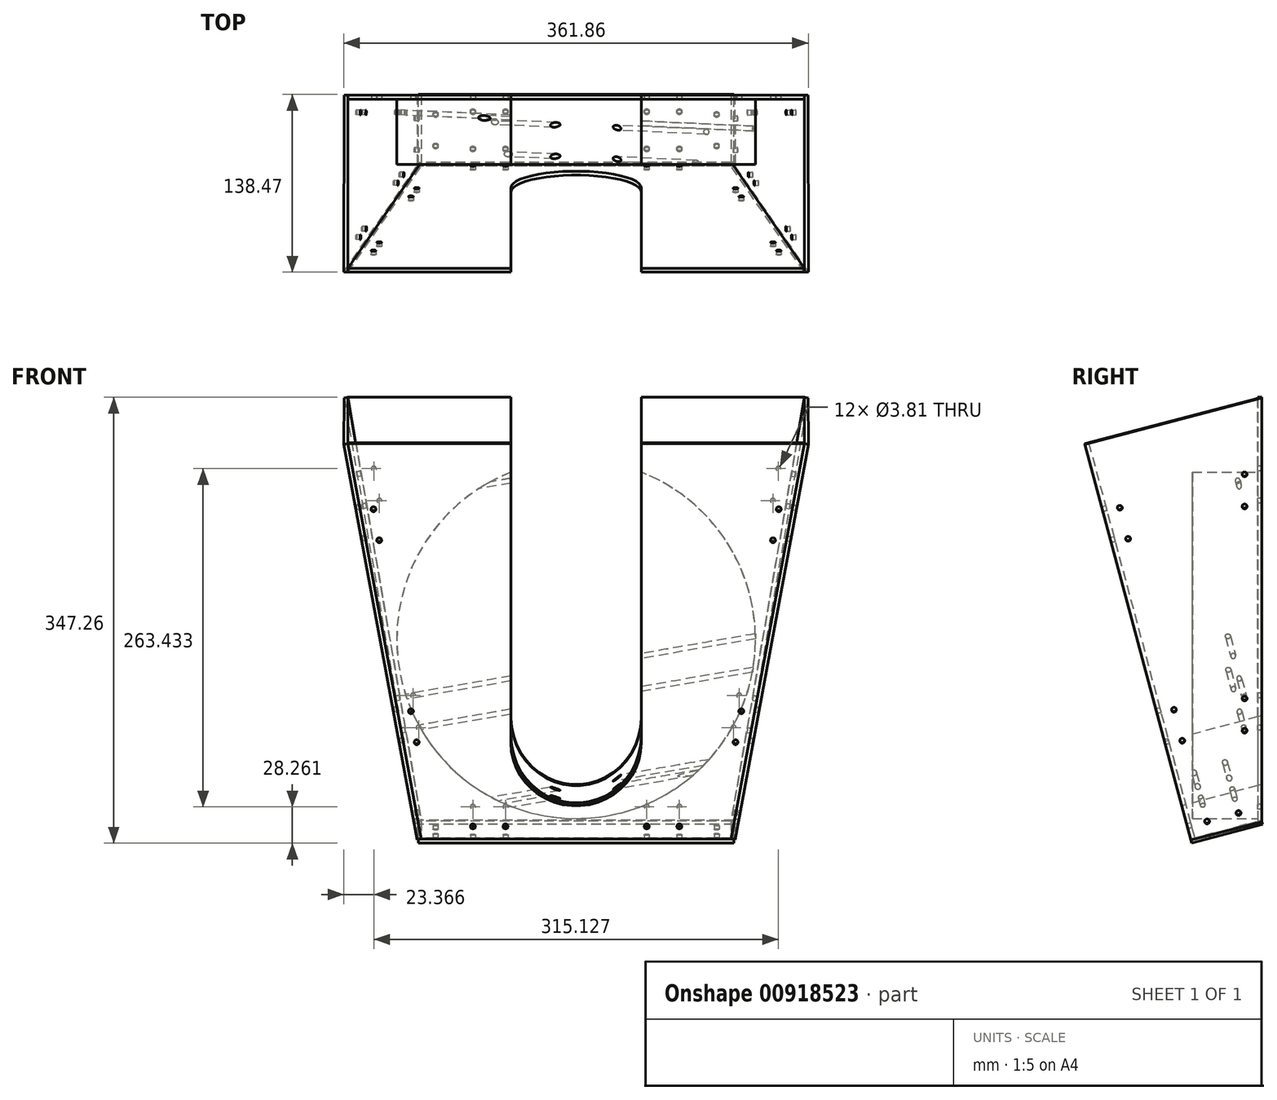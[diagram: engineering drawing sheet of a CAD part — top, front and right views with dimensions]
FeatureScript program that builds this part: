
annotation { "Feature Type Name" : "Feature", "Feature Type Description" : "" }
export const myFeature = defineFeature(function(context is Context, id is Id, definition is map)
    precondition{}
    {
        {
            var Q0;
            Q0=qCreatedBy(makeId("Right.planeOp"),FACE);
            var sketch = newSketch(context, id + "F0", { "sketchPlane" : qUnion([Q0])});
            skLineSegment(sketch, "E0.bottom", {"start": v(-164.52, 79.35) * mm, "end": v(-89.48, 66.12) * mm});
            skLineSegment(sketch, "E0.top", {"start": v(-67.49, 629.66) * mm, "end": v(7.56, 616.43) * mm});
            skLineSegment(sketch, "E0.left", {"start": v(-164.52, 79.35) * mm, "end": v(-67.49, 629.66) * mm});
            skLineSegment(sketch, "E0.right", {"start": v(-89.48, 66.12) * mm, "end": v(7.56, 616.43) * mm});
            skLineSegment(sketch, "E1.bottom", {"start": v(0, 38.1) * mm, "end": v(406.4, 38.1) * mm});
            skLineSegment(sketch, "E1.top", {"start": v(0, 546.1) * mm, "end": v(406.4, 546.1) * mm});
            skLineSegment(sketch, "E1.left", {"start": v(0, 38.1) * mm, "end": v(0, 546.1) * mm});
            skLineSegment(sketch, "E1.right", {"start": v(406.4, 38.1) * mm, "end": v(406.4, 546.1) * mm});
            skLineSegment(sketch, "E2.bottom", {"start": v(42.48, 128.48) * mm, "end": v(86.93, 128.48) * mm});
            skLineSegment(sketch, "E2.top", {"start": v(42.48, 84.03) * mm, "end": v(86.93, 84.03) * mm});
            skLineSegment(sketch, "E2.left", {"start": v(42.48, 128.48) * mm, "end": v(42.48, 84.03) * mm});
            skLineSegment(sketch, "E2.right", {"start": v(86.93, 128.48) * mm, "end": v(86.93, 84.03) * mm});
            skPoint(sketch, "E2.middle", {"position": v(64.7, 106.26) * mm});
            skSolve(sketch);
        }
        {
            var Q0;
            Q0=qCreatedBy(makeId("Front.planeOp"),FACE);
            var sketch = newSketch(context, id + "F1", { "sketchPlane" : qUnion([Q0])});
            skLineSegment(sketch, "E3.bottom", {"start": v(177.8, 596.9) * mm, "end": v(-177.8, 596.9) * mm});
            skLineSegment(sketch, "E3.top", {"start": v(120.65, 266.7) * mm, "end": v(-120.65, 266.7) * mm});
            skPoint(sketch, "E3.middle", {"position": v(0, 431.8) * mm});
            skLineSegment(sketch, "E4", {"start": v(-177.8, 596.9) * mm, "end": v(-120.65, 266.7) * mm});
            skLineSegment(sketch, "E5", {"start": v(0, 596.9) * mm, "end": v(0, 604.14) * mm, "construction": true});
            skPoint(sketch, "E5.endSnap0", {"position": v(0, 596.9) * mm});
            skLineSegment(sketch, "E6.MirrorCS", {"start": v(177.8, 596.9) * mm, "end": v(120.65, 266.7) * mm});
            skCircle(sketch, "E7", {"center": v(0, 408.44) * mm, "radius": 139.7 * mm, "construction": true});
            skCircle(sketch, "E8", {"center": v(0, 330.2) * mm, "radius": 17.46 * mm, "construction": true});
            skPoint(sketch, "E3.left.end.orphan", {"position": v(177.8, 266.7) * mm});
            skPoint(sketch, "E9.orphan", {"position": v(-177.8, 266.7) * mm});
            skSolve(sketch);
        }
        {
            var Q0;
            Q0=qSketchRegion(id+"F1",true);
            extrude(context, id + "F2", {"entities" : qUnion([Q0]), "oppositeDirection" : true, "depth" : 3.17 * mm});
        }
        {
            var Q0;
            Q0=makeQuery(id+"F1.imprint","IMPRINT",FACE,{"disambiguationData":[TD([[makeQuery(id+"F1.imprint","IMPRINT",EDGE,{"derivedFrom":sQuery(id+"F1.wireOp",EDGE,"E3.bottom")}),1.0]])]});
            var sketch = newSketch(context, id + "F3", { "sketchPlane" : qUnion([Q0])});
            skCircle(sketch, "E10.0", {"center": v(0, 408.44) * mm, "radius": 139.7 * mm});
            skSolve(sketch);
        }
        {
            var Q0;
            Q0=qSketchRegion(id+"F3",true);
            extrude(context, id + "F4", {"entities" : qUnion([Q0]), "depth" : 50.8 * mm});
        }
        {
            var Q0;
            Q0=makeQuery(id+"F4.opExtrude","CAP_FACE",FACE,{"disambiguationData":[OSD([sQuery(id+"F3.wireOp",EDGE,"E10.0")])],"isStart":false});
            var Q1;
            Q1=sQuery(id+"F1.wireOp",EDGE,"E3.top");
            cPlane(context, id + "F5", {"entities" : qUnion([Q0, Q1]), "cplaneType" : CPlaneType.LINE_ANGLE, "offset" : 25.4 * mm, "angle" : 345 * degree, "width" : 152.4 * mm, "height" : 152.4 * mm});
        }
        {
            var Q0;
            Q0=qCreatedBy(id+"F5.planeOp",FACE);
            cPlane(context, id + "F6", {"entities" : qUnion([Q0]), "cplaneType" : CPlaneType.OFFSET, "offset" : 53.97 * mm, "oppositeDirection" : true, "width" : 152.4 * mm, "height" : 152.4 * mm});
        }
        {
            var Q0;
            Q0=qCreatedBy(id+"F6.planeOp",FACE);
            var sketch = newSketch(context, id + "F7", { "sketchPlane" : qUnion([Q0])});
            skLineSegment(sketch, "E11.0", {"start": v(177.8, 576.56) * mm, "end": v(120.65, 257.61) * mm});
            skLineSegment(sketch, "E11.1", {"start": v(-177.8, 576.56) * mm, "end": v(177.8, 576.56) * mm});
            skLineSegment(sketch, "E11.2", {"start": v(-177.8, 576.56) * mm, "end": v(-120.65, 257.61) * mm});
            skLineSegment(sketch, "E11.3", {"start": v(-120.65, 257.61) * mm, "end": v(120.65, 257.61) * mm});
            skSolve(sketch);
        }
        {
            var Q0;
            Q0=makeQuery(id+"F7.imprint","IMPRINT",FACE,{"disambiguationData":[TD([[makeQuery(id+"F7.imprint","IMPRINT",EDGE,{"derivedFrom":sQuery(id+"F7.wireOp",EDGE,"E11.0")}),-1.0]])]});
            extrude(context, id + "F8", {"entities" : qUnion([Q0]), "depth" : 3.17 * mm});
        }
        {
            var Q0;
            Q0=makeQuery(id+"F8.opExtrude","SWEPT_FACE",FACE,{"disambiguationData":[OSD([sQuery(id+"F7.wireOp",EDGE,"E11.0")])]});
            var sketch = newSketch(context, id + "F9", { "sketchPlane" : qUnion([Q0])});
            skLineSegment(sketch, "E12.0", {"start": v(0.18, 618.48) * mm, "end": v(0.18, 283.37) * mm});
            skLineSegment(sketch, "E13.0", {"start": v(138.18, 582.92) * mm, "end": v(55.54, 269.6) * mm});
            skLineSegment(sketch, "E14", {"start": v(0.18, 283.37) * mm, "end": v(52.47, 270.41) * mm});
            skLineSegment(sketch, "E15", {"start": v(0.18, 618.48) * mm, "end": v(138.18, 582.92) * mm});
            skSolve(sketch);
        }
        {
            var Q0;
            {var subQ0=sQuery(id+"F9.wireOp",EDGE,"E12.0");Q0=makeQuery(id+"F9.imprint","IMPRINT",FACE,{"disambiguationData":[TD([[makeQuery(id+"F9.imprint","IMPRINT",EDGE,{"derivedFrom":subQ0}),1.0]])]});}
            var Q1;
            {var subQ0=sQuery(id+"F9.wireOp",EDGE,"E13.0");Q1=makeQuery(id+"F9.imprint","IMPRINT",FACE,{"disambiguationData":[TD([[makeQuery(id+"F9.imprint","IMPRINT",EDGE,{"derivedFrom":subQ0}),-1.0]])]});}
            extrude(context, id + "F10", {"entities" : qUnion([Q0, Q1]), "depth" : 3.17 * mm});
        }
        {
            var Q0;
            Q0=makeQuery(id+"F10.opExtrude","SWEPT_BODY",BODY,{"disambiguationData":[OSD([sQuery(id+"F7.wireOp",EDGE,"E11.0"),sQuery(id+"F9.wireOp",EDGE,"E12.0"),sQuery(id+"F9.wireOp",EDGE,"E14"),sQuery(id+"F9.wireOp",EDGE,"E15")])]});
            var Q1;
            Q1=qCreatedBy(makeId("Right.planeOp"),FACE);
            mirror(context, id + "F11", {"entities" : qUnion([Q0]), "mirrorPlane" : qUnion([Q1])});
        }
        {
            var Q0;
            Q0=makeQuery(id+"F8.opExtrude","SWEPT_FACE",FACE,{"disambiguationData":[OSD([sQuery(id+"F7.wireOp",EDGE,"E11.3")])]});
            var sketch = newSketch(context, id + "F12", { "sketchPlane" : qUnion([Q0])});
            skLineSegment(sketch, "E16.bottom", {"start": v(122.9, -15.05) * mm, "end": v(-122.9, -15.05) * mm});
            skLineSegment(sketch, "E16.top", {"start": v(122.9, -72.1) * mm, "end": v(-122.9, -72.1) * mm});
            skLineSegment(sketch, "E16.left", {"start": v(122.9, -15.05) * mm, "end": v(122.9, -72.1) * mm});
            skLineSegment(sketch, "E16.right", {"start": v(-122.9, -15.05) * mm, "end": v(-122.9, -72.1) * mm});
            skPoint(sketch, "E16.middle", {"position": v(0, -43.57) * mm});
            skSolve(sketch);
        }
        {
            var Q0;
            Q0=qSketchRegion(id+"F12",true);
            extrude(context, id + "F13", {"entities" : qUnion([Q0]), "depth" : 3.17 * mm});
        }
        {
            var Q0;
            Q0=makeQuery(id+"F8.opExtrude","CAP_FACE",FACE,{"disambiguationData":[OSD([sQuery(id+"F7.wireOp",EDGE,"E11.0"),sQuery(id+"F7.wireOp",EDGE,"E11.1"),sQuery(id+"F7.wireOp",EDGE,"E11.2"),sQuery(id+"F7.wireOp",EDGE,"E11.3")])],"isStart":true});
            var sketch = newSketch(context, id + "F14", { "sketchPlane" : qUnion([Q0])});
            skLineSegment(sketch, "E17", {"start": v(0, 439.09) * mm, "end": v(0, 333.36) * mm, "construction": true});
            skLineSegment(sketch, "E18.bottom", {"start": v(-170.23, 534.32) * mm, "end": v(-149.92, 537.96) * mm, "construction": true});
            skLineSegment(sketch, "E18.top", {"start": v(-161.27, 484.32) * mm, "end": v(-140.96, 487.96) * mm, "construction": true});
            skLineSegment(sketch, "E18.left", {"start": v(-170.23, 534.32) * mm, "end": v(-161.27, 484.32) * mm, "construction": true});
            skLineSegment(sketch, "E18.right", {"start": v(-149.92, 537.96) * mm, "end": v(-140.96, 487.96) * mm, "construction": true});
            skLineSegment(sketch, "E19.bottom", {"start": v(-93.12, 278.25) * mm, "end": v(-42.32, 278.25) * mm, "construction": true});
            skLineSegment(sketch, "E19.top", {"start": v(-93.12, 257.61) * mm, "end": v(-42.32, 257.61) * mm});
            skLineSegment(sketch, "E19.left", {"start": v(-93.12, 278.25) * mm, "end": v(-93.12, 257.61) * mm, "construction": true});
            skLineSegment(sketch, "E19.right", {"start": v(-42.32, 278.25) * mm, "end": v(-42.32, 257.61) * mm, "construction": true});
            skLineSegment(sketch, "E20", {"start": v(-160.07, 536.14) * mm, "end": v(-151.11, 486.14) * mm, "construction": true});
            skLineSegment(sketch, "E21", {"start": v(-93.12, 267.93) * mm, "end": v(-42.32, 267.93) * mm, "construction": true});
            skLineSegment(sketch, "E22", {"start": v(-145.44, 512.96) * mm, "end": v(-165.75, 509.32) * mm, "construction": true});
            skLineSegment(sketch, "E23", {"start": v(-67.72, 278.25) * mm, "end": v(-67.72, 257.61) * mm, "construction": true});
            skCircle(sketch, "E24", {"center": v(-157.83, 523.64) * mm, "radius": 1.9 * mm});
            skCircle(sketch, "E25.MirrorC", {"center": v(-153.35, 498.64) * mm, "radius": 1.9 * mm});
            skLineSegment(sketch, "E26.bottom", {"start": v(-141.04, 371.42) * mm, "end": v(-120.73, 375.06) * mm, "construction": true});
            skLineSegment(sketch, "E26.top", {"start": v(-132.08, 321.41) * mm, "end": v(-111.77, 325.05) * mm, "construction": true});
            skLineSegment(sketch, "E26.left", {"start": v(-141.04, 371.42) * mm, "end": v(-132.08, 321.41) * mm, "construction": true});
            skLineSegment(sketch, "E26.right", {"start": v(-120.73, 375.06) * mm, "end": v(-111.77, 325.05) * mm, "construction": true});
            skLineSegment(sketch, "E27", {"start": v(-130.88, 373.24) * mm, "end": v(-121.92, 323.23) * mm, "construction": true});
            skLineSegment(sketch, "E28", {"start": v(-116.25, 350.05) * mm, "end": v(-136.56, 346.41) * mm, "construction": true});
            skCircle(sketch, "E29", {"center": v(-128.64, 360.73) * mm, "radius": 1.9 * mm});
            skCircle(sketch, "E30.MirrorC", {"center": v(-124.16, 335.73) * mm, "radius": 1.9 * mm});
            skCircle(sketch, "E31", {"center": v(-80.42, 267.93) * mm, "radius": 1.9 * mm});
            skCircle(sketch, "E32.MirrorC", {"center": v(-55.02, 267.93) * mm, "radius": 1.9 * mm});
            skLineSegment(sketch, "E33.MirrorCS", {"start": v(132.08, 321.41) * mm, "end": v(111.77, 325.05) * mm, "construction": true});
            skCircle(sketch, "E34.MirrorC", {"center": v(128.64, 360.73) * mm, "radius": 1.9 * mm});
            skCircle(sketch, "E35.MirrorC", {"center": v(157.83, 523.64) * mm, "radius": 1.9 * mm});
            skLineSegment(sketch, "E36.MirrorCS", {"start": v(42.32, 278.25) * mm, "end": v(42.32, 257.61) * mm, "construction": true});
            skLineSegment(sketch, "E37.MirrorCS", {"start": v(93.12, 278.25) * mm, "end": v(93.12, 257.61) * mm, "construction": true});
            skLineSegment(sketch, "E38.MirrorCS", {"start": v(161.27, 484.32) * mm, "end": v(140.96, 487.96) * mm, "construction": true});
            skCircle(sketch, "E39.MirrorC", {"center": v(55.02, 267.93) * mm, "radius": 1.9 * mm});
            skLineSegment(sketch, "E40.MirrorCS", {"start": v(145.44, 512.96) * mm, "end": v(165.75, 509.32) * mm, "construction": true});
            skLineSegment(sketch, "E41.MirrorCS", {"start": v(170.23, 534.32) * mm, "end": v(149.92, 537.96) * mm, "construction": true});
            skLineSegment(sketch, "E42.MirrorCS", {"start": v(130.88, 373.24) * mm, "end": v(121.92, 323.23) * mm, "construction": true});
            skCircle(sketch, "E43.MirrorC", {"center": v(124.16, 335.73) * mm, "radius": 1.9 * mm});
            skLineSegment(sketch, "E44.MirrorCS", {"start": v(160.07, 536.14) * mm, "end": v(151.11, 486.14) * mm, "construction": true});
            skLineSegment(sketch, "E45.MirrorCS", {"start": v(141.04, 371.42) * mm, "end": v(120.73, 375.06) * mm, "construction": true});
            skCircle(sketch, "E46.MirrorC", {"center": v(153.35, 498.64) * mm, "radius": 1.9 * mm});
            skCircle(sketch, "E47.MirrorC", {"center": v(80.42, 267.93) * mm, "radius": 1.9 * mm});
            skLineSegment(sketch, "E48.MirrorCS", {"start": v(141.04, 371.42) * mm, "end": v(132.08, 321.41) * mm, "construction": true});
            skLineSegment(sketch, "E49.MirrorCS", {"start": v(93.12, 257.61) * mm, "end": v(42.32, 257.61) * mm});
            skLineSegment(sketch, "E50.MirrorCS", {"start": v(116.25, 350.05) * mm, "end": v(136.56, 346.41) * mm, "construction": true});
            skLineSegment(sketch, "E51.MirrorCS", {"start": v(170.23, 534.32) * mm, "end": v(161.27, 484.32) * mm, "construction": true});
            skLineSegment(sketch, "E52.MirrorCS", {"start": v(149.92, 537.96) * mm, "end": v(140.96, 487.96) * mm, "construction": true});
            skLineSegment(sketch, "E53.MirrorCS", {"start": v(120.73, 375.06) * mm, "end": v(111.77, 325.05) * mm, "construction": true});
            skLineSegment(sketch, "E54.MirrorCS", {"start": v(93.12, 267.93) * mm, "end": v(42.32, 267.93) * mm, "construction": true});
            skLineSegment(sketch, "E55.MirrorCS", {"start": v(67.72, 278.25) * mm, "end": v(67.72, 257.61) * mm, "construction": true});
            skLineSegment(sketch, "E56.MirrorCS", {"start": v(93.12, 278.25) * mm, "end": v(42.32, 278.25) * mm, "construction": true});
            skSolve(sketch);
        }
        {
            var Q0;
            Q0=qSketchRegion(id+"F14",true);
            var Q1;
            Q1=makeQuery(id+"F8.opExtrude","CAP_FACE",FACE,{"disambiguationData":[OSD([sQuery(id+"F7.wireOp",EDGE,"E11.0"),sQuery(id+"F7.wireOp",EDGE,"E11.1"),sQuery(id+"F7.wireOp",EDGE,"E11.2"),sQuery(id+"F7.wireOp",EDGE,"E11.3")])],"isStart":false});
            extrude(context, id + "F15", {"entities" : qUnion([Q0]), "operationType" : NewBodyOperationType.REMOVE, "endBound" : BoundingType.UP_TO_SURFACE, "oppositeDirection" : true, "depth" : 25.4 * mm, "endBoundEntityFace" : qUnion([Q1]), "offsetDistance" : 25.4 * mm});
        }
        {
            var Q0;
            Q0=makeQuery(id+"F10.opExtrude","CAP_FACE",FACE,{"disambiguationData":[OSD([sQuery(id+"F7.wireOp",EDGE,"E11.0"),sQuery(id+"F7.wireOp",EDGE,"E11.3"),sQuery(id+"F9.wireOp",EDGE,"E12.0"),sQuery(id+"F9.wireOp",EDGE,"E13.0"),sQuery(id+"F9.wireOp",EDGE,"E14"),sQuery(id+"F9.wireOp",EDGE,"E15")])],"isStart":false});
            var sketch = newSketch(context, id + "F16", { "sketchPlane" : qUnion([Q0])});
            skLineSegment(sketch, "E57.0", {"start": v(127.23, 541.42) * mm, "end": v(114.28, 492.3) * mm, "construction": true});
            skLineSegment(sketch, "E58.0", {"start": v(85.03, 381.4) * mm, "end": v(72.07, 332.28) * mm, "construction": true});
            skLineSegment(sketch, "E59.bottom", {"start": v(62, 387.47) * mm, "end": v(85.03, 381.4) * mm, "construction": true});
            skLineSegment(sketch, "E59.top", {"start": v(49.05, 338.35) * mm, "end": v(72.07, 332.28) * mm, "construction": true});
            skLineSegment(sketch, "E59.left", {"start": v(62, 387.47) * mm, "end": v(49.05, 338.35) * mm, "construction": true});
            skLineSegment(sketch, "E60", {"start": v(81.96, 382.2) * mm, "end": v(69, 333.09) * mm, "construction": true});
            skPoint(sketch, "E61", {"position": v(71.98, 384.84) * mm});
            skLineSegment(sketch, "E62", {"start": v(71.98, 384.84) * mm, "end": v(59.02, 335.72) * mm, "construction": true});
            skLineSegment(sketch, "E63", {"start": v(55.52, 362.9) * mm, "end": v(75.48, 357.65) * mm, "construction": true});
            skCircle(sketch, "E64", {"center": v(62.26, 348) * mm, "radius": 1.9 * mm});
            skCircle(sketch, "E65.MirrorC", {"center": v(68.74, 372.56) * mm, "radius": 1.9 * mm});
            skLineSegment(sketch, "E66.bottom", {"start": v(104.2, 547.5) * mm, "end": v(127.23, 541.42) * mm, "construction": true});
            skLineSegment(sketch, "E66.top", {"start": v(91.25, 498.37) * mm, "end": v(114.28, 492.3) * mm, "construction": true});
            skLineSegment(sketch, "E66.left", {"start": v(104.2, 547.5) * mm, "end": v(91.25, 498.37) * mm, "construction": true});
            skLineSegment(sketch, "E67", {"start": v(124.16, 542.23) * mm, "end": v(111.2, 493.11) * mm, "construction": true});
            skPoint(sketch, "E68", {"position": v(114.18, 544.86) * mm});
            skLineSegment(sketch, "E69", {"start": v(114.18, 544.86) * mm, "end": v(101.23, 495.74) * mm, "construction": true});
            skLineSegment(sketch, "E70", {"start": v(97.73, 522.93) * mm, "end": v(117.68, 517.67) * mm, "construction": true});
            skCircle(sketch, "E71", {"center": v(104.47, 508.02) * mm, "radius": 1.9 * mm});
            skCircle(sketch, "E72.MirrorC", {"center": v(110.95, 532.58) * mm, "radius": 1.9 * mm});
            skLineSegment(sketch, "E73.bottom", {"start": v(3.35, 570.93) * mm, "end": v(24, 570.93) * mm, "construction": true});
            skLineSegment(sketch, "E73.top", {"start": v(3.35, 520.13) * mm, "end": v(24, 520.13) * mm, "construction": true});
            skLineSegment(sketch, "E73.left", {"start": v(3.35, 570.93) * mm, "end": v(3.35, 520.13) * mm, "construction": true});
            skLineSegment(sketch, "E73.right", {"start": v(24, 570.93) * mm, "end": v(24, 520.13) * mm, "construction": true});
            skLineSegment(sketch, "E74.bottom", {"start": v(3.35, 570.93) * mm, "end": v(0.18, 570.93) * mm, "construction": true});
            skLineSegment(sketch, "E74.top", {"start": v(3.35, 520.13) * mm, "end": v(0.18, 520.13) * mm, "construction": true});
            skLineSegment(sketch, "E74.right", {"start": v(0.18, 570.93) * mm, "end": v(0.18, 520.13) * mm, "construction": true});
            skLineSegment(sketch, "E75", {"start": v(13.67, 570.93) * mm, "end": v(13.67, 520.13) * mm, "construction": true});
            skLineSegment(sketch, "E76", {"start": v(24, 545.53) * mm, "end": v(3.35, 545.53) * mm, "construction": true});
            skCircle(sketch, "E77", {"center": v(13.67, 558.23) * mm, "radius": 1.9 * mm});
            skCircle(sketch, "E78.MirrorC", {"center": v(13.67, 532.83) * mm, "radius": 1.9 * mm});
            skLineSegment(sketch, "E79.bottom", {"start": v(3.35, 393.68) * mm, "end": v(24, 393.68) * mm, "construction": true});
            skLineSegment(sketch, "E79.top", {"start": v(3.35, 342.88) * mm, "end": v(24, 342.88) * mm, "construction": true});
            skLineSegment(sketch, "E79.left", {"start": v(3.35, 393.68) * mm, "end": v(3.35, 342.88) * mm, "construction": true});
            skLineSegment(sketch, "E79.right", {"start": v(24, 393.68) * mm, "end": v(24, 342.88) * mm, "construction": true});
            skLineSegment(sketch, "E80.bottom", {"start": v(3.35, 393.68) * mm, "end": v(0.18, 393.68) * mm, "construction": true});
            skLineSegment(sketch, "E80.top", {"start": v(3.35, 342.88) * mm, "end": v(0.18, 342.88) * mm, "construction": true});
            skLineSegment(sketch, "E80.right", {"start": v(0.18, 393.68) * mm, "end": v(0.18, 342.88) * mm, "construction": true});
            skLineSegment(sketch, "E81", {"start": v(13.67, 393.68) * mm, "end": v(13.67, 342.88) * mm, "construction": true});
            skLineSegment(sketch, "E82", {"start": v(24, 368.28) * mm, "end": v(3.35, 368.28) * mm, "construction": true});
            skCircle(sketch, "E83", {"center": v(13.67, 380.98) * mm, "radius": 1.9 * mm});
            skCircle(sketch, "E84.MirrorC", {"center": v(13.67, 355.58) * mm, "radius": 1.9 * mm});
            skLineSegment(sketch, "E85.bottom", {"start": v(8.73, 303.76) * mm, "end": v(57.85, 290.8) * mm, "construction": true});
            skLineSegment(sketch, "E85.top", {"start": v(3.46, 283.8) * mm, "end": v(52.58, 270.85) * mm, "construction": true});
            skLineSegment(sketch, "E85.left", {"start": v(8.73, 303.76) * mm, "end": v(3.46, 283.8) * mm, "construction": true});
            skLineSegment(sketch, "E85.right", {"start": v(57.85, 290.8) * mm, "end": v(52.58, 270.85) * mm, "construction": true});
            skLineSegment(sketch, "E86.top", {"start": v(2.65, 280.73) * mm, "end": v(51.77, 267.78) * mm, "construction": true});
            skLineSegment(sketch, "E86.left", {"start": v(3.46, 283.8) * mm, "end": v(2.65, 280.73) * mm, "construction": true});
            skLineSegment(sketch, "E86.right", {"start": v(52.58, 270.85) * mm, "end": v(51.77, 267.78) * mm, "construction": true});
            skLineSegment(sketch, "E87", {"start": v(6.1, 293.78) * mm, "end": v(55.22, 280.82) * mm, "construction": true});
            skLineSegment(sketch, "E88", {"start": v(33.29, 297.28) * mm, "end": v(28.02, 277.32) * mm, "construction": true});
            skCircle(sketch, "E89", {"center": v(18.38, 290.54) * mm, "radius": 1.9 * mm});
            skCircle(sketch, "E90.MirrorC", {"center": v(42.94, 284.06) * mm, "radius": 1.9 * mm});
            skSolve(sketch);
        }
        {
            var Q0;
            Q0=qSketchRegion(id+"F16",true);
            extrude(context, id + "F17", {"entities" : qUnion([Q0]), "operationType" : NewBodyOperationType.REMOVE, "endBound" : BoundingType.THROUGH_ALL, "oppositeDirection" : true, "depth" : 25.4 * mm, "offsetDistance" : 25.4 * mm});
        }
        {
            var Q0;
            Q0=makeQuery(id+"F11.opPattern","COPY",BODY,{"derivedFrom":makeQuery(id+"F10.opExtrude","SWEPT_BODY",BODY,{"disambiguationData":[OSD([sQuery(id+"F7.wireOp",EDGE,"E11.0"),sQuery(id+"F7.wireOp",EDGE,"E11.3"),sQuery(id+"F9.wireOp",EDGE,"E12.0"),sQuery(id+"F9.wireOp",EDGE,"E13.0"),sQuery(id+"F9.wireOp",EDGE,"E14"),sQuery(id+"F9.wireOp",EDGE,"E15")])]}),"instanceName":"1"});
            deleteBodies(context, id + "F18", {"entities" : qUnion([Q0])});
        }
        {
            var Q0;
            Q0=makeQuery(id+"F10.opExtrude","SWEPT_BODY",BODY,{"disambiguationData":[OSD([sQuery(id+"F7.wireOp",EDGE,"E11.0"),sQuery(id+"F7.wireOp",EDGE,"E11.3"),sQuery(id+"F9.wireOp",EDGE,"E12.0"),sQuery(id+"F9.wireOp",EDGE,"E13.0"),sQuery(id+"F9.wireOp",EDGE,"E14"),sQuery(id+"F9.wireOp",EDGE,"E15")])]});
            var Q1;
            Q1=qCreatedBy(makeId("Right.planeOp"),FACE);
            mirror(context, id + "F19", {"entities" : qUnion([Q0]), "mirrorPlane" : qUnion([Q1])});
        }
        {
            var Q0;
            Q0=makeQuery(id+"F1.imprint","IMPRINT",FACE,{"disambiguationData":[TD([[makeQuery(id+"F1.imprint","IMPRINT",EDGE,{"derivedFrom":sQuery(id+"F1.wireOp",EDGE,"E3.bottom")}),1.0]])]});
            var sketch = newSketch(context, id + "F20", { "sketchPlane" : qUnion([Q0])});
            skLineSegment(sketch, "E91.0", {"start": v(-172.82, 549.5) * mm, "end": v(-164.15, 499.45) * mm, "construction": true});
            skLineSegment(sketch, "E92.bottom", {"start": v(-169.9, 552.1) * mm, "end": v(-173.03, 551.57) * mm, "construction": true});
            skLineSegment(sketch, "E92.top", {"start": v(-161.23, 502.05) * mm, "end": v(-164.36, 501.51) * mm, "construction": true});
            skLineSegment(sketch, "E92.left", {"start": v(-169.9, 552.1) * mm, "end": v(-161.23, 502.05) * mm, "construction": true});
            skLineSegment(sketch, "E92.right", {"start": v(-173.03, 551.57) * mm, "end": v(-164.36, 501.51) * mm, "construction": true});
            skLineSegment(sketch, "E93.bottom", {"start": v(-149.56, 555.63) * mm, "end": v(-169.9, 552.1) * mm, "construction": true});
            skLineSegment(sketch, "E93.top", {"start": v(-140.9, 505.57) * mm, "end": v(-161.23, 502.05) * mm, "construction": true});
            skLineSegment(sketch, "E93.left", {"start": v(-149.56, 555.63) * mm, "end": v(-140.9, 505.57) * mm, "construction": true});
            skLineSegment(sketch, "E94", {"start": v(-159.73, 553.87) * mm, "end": v(-151.07, 503.81) * mm, "construction": true});
            skLineSegment(sketch, "E95", {"start": v(-145.23, 530.6) * mm, "end": v(-165.57, 527.08) * mm, "construction": true});
            skCircle(sketch, "E96", {"center": v(-157.56, 541.35) * mm, "radius": 1.9 * mm});
            skCircle(sketch, "E97.MirrorC", {"center": v(-153.23, 516.33) * mm, "radius": 1.9 * mm});
            skLineSegment(sketch, "E98", {"start": v(0, 542.09) * mm, "end": v(0, 433.89) * mm, "construction": true});
            skLineSegment(sketch, "E99.0", {"start": v(-137.98, 349.1) * mm, "end": v(-129.32, 299.04) * mm, "construction": true});
            skLineSegment(sketch, "E100.bottom", {"start": v(-139.32, 375.42) * mm, "end": v(-142.45, 374.88) * mm, "construction": true});
            skLineSegment(sketch, "E100.top", {"start": v(-130.65, 325.37) * mm, "end": v(-133.78, 324.83) * mm, "construction": true});
            skLineSegment(sketch, "E100.left", {"start": v(-139.32, 375.42) * mm, "end": v(-130.65, 325.37) * mm, "construction": true});
            skLineSegment(sketch, "E100.right", {"start": v(-142.45, 374.88) * mm, "end": v(-133.78, 324.83) * mm, "construction": true});
            skLineSegment(sketch, "E101.bottom", {"start": v(-118.98, 378.94) * mm, "end": v(-139.32, 375.42) * mm, "construction": true});
            skLineSegment(sketch, "E101.top", {"start": v(-110.32, 328.89) * mm, "end": v(-130.65, 325.37) * mm, "construction": true});
            skLineSegment(sketch, "E101.left", {"start": v(-118.98, 378.94) * mm, "end": v(-110.32, 328.89) * mm, "construction": true});
            skLineSegment(sketch, "E102", {"start": v(-129.15, 377.18) * mm, "end": v(-120.49, 327.13) * mm, "construction": true});
            skLineSegment(sketch, "E103", {"start": v(-114.65, 353.92) * mm, "end": v(-134.99, 350.4) * mm, "construction": true});
            skCircle(sketch, "E104", {"center": v(-126.98, 364.67) * mm, "radius": 1.9 * mm});
            skCircle(sketch, "E105.MirrorC", {"center": v(-122.65, 339.64) * mm, "radius": 1.9 * mm});
            skLineSegment(sketch, "E106.bottom", {"start": v(-42.32, 288.24) * mm, "end": v(-93.12, 288.24) * mm, "construction": true});
            skLineSegment(sketch, "E106.top", {"start": v(-42.32, 267.6) * mm, "end": v(-93.12, 267.6) * mm, "construction": true});
            skLineSegment(sketch, "E106.left", {"start": v(-42.32, 288.24) * mm, "end": v(-42.32, 267.6) * mm, "construction": true});
            skLineSegment(sketch, "E106.right", {"start": v(-93.12, 288.24) * mm, "end": v(-93.12, 267.6) * mm, "construction": true});
            skLineSegment(sketch, "E107.top", {"start": v(-42.32, 264.43) * mm, "end": v(-93.12, 264.43) * mm, "construction": true});
            skLineSegment(sketch, "E107.left", {"start": v(-42.32, 267.6) * mm, "end": v(-42.32, 264.43) * mm, "construction": true});
            skLineSegment(sketch, "E107.right", {"start": v(-93.12, 267.6) * mm, "end": v(-93.12, 264.43) * mm, "construction": true});
            skLineSegment(sketch, "E108", {"start": v(-42.32, 277.92) * mm, "end": v(-93.12, 277.92) * mm, "construction": true});
            skLineSegment(sketch, "E109", {"start": v(-67.72, 288.24) * mm, "end": v(-67.72, 267.6) * mm, "construction": true});
            skCircle(sketch, "E110", {"center": v(-55.02, 277.92) * mm, "radius": 1.9 * mm});
            skCircle(sketch, "E111.MirrorC", {"center": v(-80.42, 277.92) * mm, "radius": 1.9 * mm});
            skLineSegment(sketch, "E112.MirrorCS", {"start": v(161.23, 502.05) * mm, "end": v(164.36, 501.51) * mm, "construction": true});
            skLineSegment(sketch, "E113.MirrorCS", {"start": v(169.9, 552.1) * mm, "end": v(173.03, 551.57) * mm, "construction": true});
            skLineSegment(sketch, "E114.MirrorCS", {"start": v(139.32, 375.42) * mm, "end": v(142.45, 374.88) * mm, "construction": true});
            skLineSegment(sketch, "E115.MirrorCS", {"start": v(130.65, 325.37) * mm, "end": v(133.78, 324.83) * mm, "construction": true});
            skLineSegment(sketch, "E116.MirrorCS", {"start": v(42.32, 267.6) * mm, "end": v(42.32, 264.43) * mm, "construction": true});
            skLineSegment(sketch, "E117.MirrorCS", {"start": v(93.12, 267.6) * mm, "end": v(93.12, 264.43) * mm, "construction": true});
            skLineSegment(sketch, "E118.MirrorCS", {"start": v(139.32, 375.42) * mm, "end": v(130.65, 325.37) * mm, "construction": true});
            skCircle(sketch, "E119.MirrorC", {"center": v(126.98, 364.67) * mm, "radius": 1.9 * mm});
            skLineSegment(sketch, "E120.MirrorCS", {"start": v(169.9, 552.1) * mm, "end": v(161.23, 502.05) * mm, "construction": true});
            skLineSegment(sketch, "E121.MirrorCS", {"start": v(172.82, 549.5) * mm, "end": v(164.15, 499.45) * mm, "construction": true});
            skLineSegment(sketch, "E122.MirrorCS", {"start": v(142.45, 374.88) * mm, "end": v(133.78, 324.83) * mm, "construction": true});
            skLineSegment(sketch, "E123.MirrorCS", {"start": v(173.03, 551.57) * mm, "end": v(164.36, 501.51) * mm, "construction": true});
            skLineSegment(sketch, "E124.MirrorCS", {"start": v(42.32, 264.43) * mm, "end": v(93.12, 264.43) * mm, "construction": true});
            skLineSegment(sketch, "E125.MirrorCS", {"start": v(129.15, 377.18) * mm, "end": v(120.49, 327.13) * mm, "construction": true});
            skLineSegment(sketch, "E126.MirrorCS", {"start": v(42.32, 288.24) * mm, "end": v(42.32, 267.6) * mm, "construction": true});
            skCircle(sketch, "E127.MirrorC", {"center": v(153.23, 516.33) * mm, "radius": 1.9 * mm});
            skLineSegment(sketch, "E128.MirrorCS", {"start": v(140.9, 505.57) * mm, "end": v(161.23, 502.05) * mm, "construction": true});
            skLineSegment(sketch, "E129.MirrorCS", {"start": v(149.56, 555.63) * mm, "end": v(169.9, 552.1) * mm, "construction": true});
            skLineSegment(sketch, "E130.MirrorCS", {"start": v(145.23, 530.6) * mm, "end": v(165.57, 527.08) * mm, "construction": true});
            skLineSegment(sketch, "E131.MirrorCS", {"start": v(118.98, 378.94) * mm, "end": v(110.32, 328.89) * mm, "construction": true});
            skLineSegment(sketch, "E132.MirrorCS", {"start": v(118.98, 378.94) * mm, "end": v(139.32, 375.42) * mm, "construction": true});
            skCircle(sketch, "E133.MirrorC", {"center": v(157.56, 541.35) * mm, "radius": 1.9 * mm});
            skLineSegment(sketch, "E134.MirrorCS", {"start": v(93.12, 288.24) * mm, "end": v(93.12, 267.6) * mm, "construction": true});
            skLineSegment(sketch, "E135.MirrorCS", {"start": v(159.73, 553.87) * mm, "end": v(151.07, 503.81) * mm, "construction": true});
            skLineSegment(sketch, "E136.MirrorCS", {"start": v(42.32, 267.6) * mm, "end": v(93.12, 267.6) * mm, "construction": true});
            skCircle(sketch, "E137.MirrorC", {"center": v(122.65, 339.64) * mm, "radius": 1.9 * mm});
            skLineSegment(sketch, "E138.MirrorCS", {"start": v(114.65, 353.92) * mm, "end": v(134.99, 350.4) * mm, "construction": true});
            skLineSegment(sketch, "E139.MirrorCS", {"start": v(110.32, 328.89) * mm, "end": v(130.65, 325.37) * mm, "construction": true});
            skLineSegment(sketch, "E140.MirrorCS", {"start": v(137.98, 349.1) * mm, "end": v(129.32, 299.04) * mm, "construction": true});
            skLineSegment(sketch, "E141.MirrorCS", {"start": v(149.56, 555.63) * mm, "end": v(140.9, 505.57) * mm, "construction": true});
            skLineSegment(sketch, "E142.MirrorCS", {"start": v(42.32, 277.92) * mm, "end": v(93.12, 277.92) * mm, "construction": true});
            skCircle(sketch, "E143.MirrorC", {"center": v(55.02, 277.92) * mm, "radius": 1.9 * mm});
            skLineSegment(sketch, "E144.MirrorCS", {"start": v(42.32, 288.24) * mm, "end": v(93.12, 288.24) * mm, "construction": true});
            skLineSegment(sketch, "E145.MirrorCS", {"start": v(67.72, 288.24) * mm, "end": v(67.72, 267.6) * mm, "construction": true});
            skCircle(sketch, "E146.MirrorC", {"center": v(80.42, 277.92) * mm, "radius": 1.9 * mm});
            skSolve(sketch);
        }
        {
            var Q0;
            Q0=qSketchRegion(id+"F20",true);
            var Q1;
            Q1=sQuery(id+"F20.wireOp",EDGE,"E96");
            var Q2;
            Q2=sQuery(id+"F20.wireOp",EDGE,"E97.MirrorC");
            var Q3;
            Q3=sQuery(id+"F20.wireOp",EDGE,"E127.MirrorC");
            var Q4;
            Q4=sQuery(id+"F20.wireOp",EDGE,"E133.MirrorC");
            var Q5;
            Q5=sQuery(id+"F20.wireOp",EDGE,"E119.MirrorC");
            var Q6;
            Q6=sQuery(id+"F20.wireOp",EDGE,"E137.MirrorC");
            var Q7;
            Q7=sQuery(id+"F20.wireOp",EDGE,"E146.MirrorC");
            var Q8;
            Q8=sQuery(id+"F20.wireOp",EDGE,"E143.MirrorC");
            var Q9;
            Q9=sQuery(id+"F20.wireOp",EDGE,"E110");
            var Q10;
            Q10=sQuery(id+"F20.wireOp",EDGE,"E111.MirrorC");
            var Q11;
            Q11=sQuery(id+"F20.wireOp",EDGE,"E104");
            var Q12;
            Q12=sQuery(id+"F20.wireOp",EDGE,"E105.MirrorC");
            var Q13;
            Q13=makeQuery(id+"F2.opExtrude","CAP_FACE",FACE,{"disambiguationData":[OSD([sQuery(id+"F1.wireOp",EDGE,"E3.bottom"),sQuery(id+"F1.wireOp",EDGE,"E3.top"),sQuery(id+"F1.wireOp",EDGE,"E4"),sQuery(id+"F1.wireOp",EDGE,"E6.MirrorCS")])],"isStart":false});
            extrude(context, id + "F21", {"entities" : qUnion([Q0]), "operationType" : NewBodyOperationType.REMOVE, "surfaceEntities" : qUnion([Q1, Q2, Q3, Q4, Q5, Q6, Q7, Q8, Q9, Q10, Q11, Q12]), "endBound" : BoundingType.UP_TO_SURFACE, "oppositeDirection" : true, "depth" : 25.4 * mm, "endBoundEntityFace" : qUnion([Q13]), "offsetDistance" : 25.4 * mm});
        }
        {
            var Q0;
            Q0=makeQuery(id+"F13.opExtrude","CAP_FACE",FACE,{"disambiguationData":[OSD([sQuery(id+"F12.wireOp",EDGE,"E16.bottom"),sQuery(id+"F12.wireOp",EDGE,"E16.top"),sQuery(id+"F12.wireOp",EDGE,"E16.left"),sQuery(id+"F12.wireOp",EDGE,"E16.right")])],"isStart":false});
            var sketch = newSketch(context, id + "F22", { "sketchPlane" : qUnion([Q0])});
            skLineSegment(sketch, "E147", {"start": v(0, -15.05) * mm, "end": v(0, -38.18) * mm, "construction": true});
            skLineSegment(sketch, "E148.bottom", {"start": v(-93.12, -18.23) * mm, "end": v(-42.32, -18.23) * mm, "construction": true});
            skLineSegment(sketch, "E148.top", {"start": v(-93.12, -38.86) * mm, "end": v(-42.32, -38.86) * mm, "construction": true});
            skLineSegment(sketch, "E148.left", {"start": v(-93.12, -18.23) * mm, "end": v(-93.12, -38.86) * mm, "construction": true});
            skLineSegment(sketch, "E148.right", {"start": v(-42.32, -18.23) * mm, "end": v(-42.32, -38.86) * mm, "construction": true});
            skLineSegment(sketch, "E149.top", {"start": v(-93.12, -15.05) * mm, "end": v(-42.32, -15.05) * mm, "construction": true});
            skLineSegment(sketch, "E149.left", {"start": v(-93.12, -18.23) * mm, "end": v(-93.12, -15.05) * mm, "construction": true});
            skLineSegment(sketch, "E149.right", {"start": v(-42.32, -18.23) * mm, "end": v(-42.32, -15.05) * mm, "construction": true});
            skLineSegment(sketch, "E150", {"start": v(-93.12, -28.55) * mm, "end": v(-42.32, -28.55) * mm, "construction": true});
            skLineSegment(sketch, "E151", {"start": v(-67.72, -38.86) * mm, "end": v(-67.72, -18.23) * mm, "construction": true});
            skCircle(sketch, "E152", {"center": v(-80.42, -28.55) * mm, "radius": 1.9 * mm});
            skCircle(sketch, "E153.MirrorC", {"center": v(-55.02, -28.55) * mm, "radius": 1.9 * mm});
            skLineSegment(sketch, "E154.bottom", {"start": v(-93.12, -48.28) * mm, "end": v(-42.32, -48.28) * mm, "construction": true});
            skLineSegment(sketch, "E154.top", {"start": v(-93.12, -68.92) * mm, "end": v(-42.32, -68.92) * mm, "construction": true});
            skLineSegment(sketch, "E154.left", {"start": v(-93.12, -48.28) * mm, "end": v(-93.12, -68.92) * mm, "construction": true});
            skLineSegment(sketch, "E154.right", {"start": v(-42.32, -48.28) * mm, "end": v(-42.32, -68.92) * mm, "construction": true});
            skLineSegment(sketch, "E155.top", {"start": v(-93.12, -72.1) * mm, "end": v(-42.32, -72.1) * mm, "construction": true});
            skLineSegment(sketch, "E155.left", {"start": v(-93.12, -68.92) * mm, "end": v(-93.12, -72.1) * mm, "construction": true});
            skLineSegment(sketch, "E155.right", {"start": v(-42.32, -68.92) * mm, "end": v(-42.32, -72.1) * mm, "construction": true});
            skLineSegment(sketch, "E156", {"start": v(-67.72, -48.28) * mm, "end": v(-67.72, -68.92) * mm, "construction": true});
            skLineSegment(sketch, "E157", {"start": v(-93.12, -58.6) * mm, "end": v(-42.32, -58.6) * mm, "construction": true});
            skCircle(sketch, "E158", {"center": v(-80.42, -58.6) * mm, "radius": 1.9 * mm});
            skCircle(sketch, "E159.MirrorC", {"center": v(-55.02, -58.6) * mm, "radius": 1.9 * mm});
            skLineSegment(sketch, "E160.bottom", {"start": v(-119.72, -18.23) * mm, "end": v(-99.09, -18.23) * mm, "construction": true});
            skLineSegment(sketch, "E160.top", {"start": v(-119.72, -69.03) * mm, "end": v(-99.09, -69.03) * mm, "construction": true});
            skLineSegment(sketch, "E160.left", {"start": v(-119.72, -18.23) * mm, "end": v(-119.72, -69.03) * mm, "construction": true});
            skLineSegment(sketch, "E160.right", {"start": v(-99.09, -18.23) * mm, "end": v(-99.09, -69.03) * mm, "construction": true});
            skLineSegment(sketch, "E161.bottom", {"start": v(-119.72, -18.23) * mm, "end": v(-122.9, -18.23) * mm, "construction": true});
            skLineSegment(sketch, "E161.top", {"start": v(-119.72, -69.03) * mm, "end": v(-122.9, -69.03) * mm, "construction": true});
            skLineSegment(sketch, "E161.right", {"start": v(-122.9, -18.23) * mm, "end": v(-122.9, -69.03) * mm, "construction": true});
            skLineSegment(sketch, "E162", {"start": v(-99.09, -43.63) * mm, "end": v(-119.72, -43.63) * mm, "construction": true});
            skLineSegment(sketch, "E163", {"start": v(-109.4, -18.23) * mm, "end": v(-109.4, -69.03) * mm, "construction": true});
            skCircle(sketch, "E164", {"center": v(-109.4, -30.93) * mm, "radius": 1.9 * mm});
            skCircle(sketch, "E165.MirrorC", {"center": v(-109.4, -56.33) * mm, "radius": 1.9 * mm});
            skLineSegment(sketch, "E166.MirrorCS", {"start": v(93.12, -18.23) * mm, "end": v(93.12, -15.05) * mm, "construction": true});
            skLineSegment(sketch, "E167.MirrorCS", {"start": v(42.32, -18.23) * mm, "end": v(42.32, -15.05) * mm, "construction": true});
            skLineSegment(sketch, "E168.MirrorCS", {"start": v(119.72, -18.23) * mm, "end": v(122.9, -18.23) * mm, "construction": true});
            skLineSegment(sketch, "E169.MirrorCS", {"start": v(119.72, -69.03) * mm, "end": v(122.9, -69.03) * mm, "construction": true});
            skLineSegment(sketch, "E170.MirrorCS", {"start": v(42.32, -68.92) * mm, "end": v(42.32, -72.1) * mm, "construction": true});
            skLineSegment(sketch, "E171.MirrorCS", {"start": v(93.12, -68.92) * mm, "end": v(93.12, -72.1) * mm, "construction": true});
            skLineSegment(sketch, "E172.MirrorCS", {"start": v(93.12, -18.23) * mm, "end": v(42.32, -18.23) * mm, "construction": true});
            skLineSegment(sketch, "E173.MirrorCS", {"start": v(119.72, -18.23) * mm, "end": v(119.72, -69.03) * mm, "construction": true});
            skLineSegment(sketch, "E174.MirrorCS", {"start": v(93.12, -68.92) * mm, "end": v(42.32, -68.92) * mm, "construction": true});
            skCircle(sketch, "E175.MirrorC", {"center": v(109.4, -30.93) * mm, "radius": 1.9 * mm});
            skLineSegment(sketch, "E176.MirrorCS", {"start": v(93.12, -38.86) * mm, "end": v(42.32, -38.86) * mm, "construction": true});
            skCircle(sketch, "E177.MirrorC", {"center": v(80.42, -58.6) * mm, "radius": 1.9 * mm});
            skLineSegment(sketch, "E178.MirrorCS", {"start": v(42.32, -48.28) * mm, "end": v(42.32, -68.92) * mm, "construction": true});
            skLineSegment(sketch, "E179.MirrorCS", {"start": v(93.12, -48.28) * mm, "end": v(93.12, -68.92) * mm, "construction": true});
            skLineSegment(sketch, "E180.MirrorCS", {"start": v(122.9, -18.23) * mm, "end": v(122.9, -69.03) * mm, "construction": true});
            skLineSegment(sketch, "E181.MirrorCS", {"start": v(119.72, -18.23) * mm, "end": v(99.09, -18.23) * mm, "construction": true});
            skLineSegment(sketch, "E182.MirrorCS", {"start": v(67.72, -48.28) * mm, "end": v(67.72, -68.92) * mm, "construction": true});
            skLineSegment(sketch, "E183.MirrorCS", {"start": v(93.12, -18.23) * mm, "end": v(93.12, -38.86) * mm, "construction": true});
            skLineSegment(sketch, "E184.MirrorCS", {"start": v(93.12, -15.05) * mm, "end": v(42.32, -15.05) * mm, "construction": true});
            skLineSegment(sketch, "E185.MirrorCS", {"start": v(42.32, -18.23) * mm, "end": v(42.32, -38.86) * mm, "construction": true});
            skCircle(sketch, "E186.MirrorC", {"center": v(55.02, -58.6) * mm, "radius": 1.9 * mm});
            skLineSegment(sketch, "E187.MirrorCS", {"start": v(119.72, -69.03) * mm, "end": v(99.09, -69.03) * mm, "construction": true});
            skLineSegment(sketch, "E188.MirrorCS", {"start": v(99.09, -43.63) * mm, "end": v(119.72, -43.63) * mm, "construction": true});
            skLineSegment(sketch, "E189.MirrorCS", {"start": v(93.12, -48.28) * mm, "end": v(42.32, -48.28) * mm, "construction": true});
            skLineSegment(sketch, "E190.MirrorCS", {"start": v(99.09, -18.23) * mm, "end": v(99.09, -69.03) * mm, "construction": true});
            skCircle(sketch, "E191.MirrorC", {"center": v(55.02, -28.55) * mm, "radius": 1.9 * mm});
            skLineSegment(sketch, "E192.MirrorCS", {"start": v(93.12, -58.6) * mm, "end": v(42.32, -58.6) * mm, "construction": true});
            skCircle(sketch, "E193.MirrorC", {"center": v(109.4, -56.33) * mm, "radius": 1.9 * mm});
            skLineSegment(sketch, "E194.MirrorCS", {"start": v(93.12, -72.1) * mm, "end": v(42.32, -72.1) * mm, "construction": true});
            skLineSegment(sketch, "E195.MirrorCS", {"start": v(67.72, -38.86) * mm, "end": v(67.72, -18.23) * mm, "construction": true});
            skCircle(sketch, "E196.MirrorC", {"center": v(80.42, -28.55) * mm, "radius": 1.9 * mm});
            skLineSegment(sketch, "E197.MirrorCS", {"start": v(93.12, -28.55) * mm, "end": v(42.32, -28.55) * mm, "construction": true});
            skLineSegment(sketch, "E198.MirrorCS", {"start": v(109.4, -18.23) * mm, "end": v(109.4, -69.03) * mm, "construction": true});
            skSolve(sketch);
        }
        {
            var Q0;
            Q0=qSketchRegion(id+"F22",true);
            var Q1;
            Q1=makeQuery(id+"F13.opExtrude","CAP_FACE",FACE,{"disambiguationData":[OSD([sQuery(id+"F12.wireOp",EDGE,"E16.bottom"),sQuery(id+"F12.wireOp",EDGE,"E16.top"),sQuery(id+"F12.wireOp",EDGE,"E16.left"),sQuery(id+"F12.wireOp",EDGE,"E16.right")])],"isStart":true});
            extrude(context, id + "F23", {"entities" : qUnion([Q0]), "operationType" : NewBodyOperationType.REMOVE, "endBound" : BoundingType.UP_TO_SURFACE, "oppositeDirection" : true, "depth" : 25.4 * mm, "endBoundEntityFace" : qUnion([Q1]), "offsetDistance" : 25.4 * mm});
        }
        {
            var Q0;
            Q0=makeQuery(id+"F8.opExtrude","CAP_FACE",FACE,{"disambiguationData":[OSD([sQuery(id+"F7.wireOp",EDGE,"E11.0"),sQuery(id+"F7.wireOp",EDGE,"E11.1"),sQuery(id+"F7.wireOp",EDGE,"E11.2"),sQuery(id+"F7.wireOp",EDGE,"E11.3")])],"isStart":true});
            var sketch = newSketch(context, id + "F24", { "sketchPlane" : qUnion([Q0])});
            skLineSegment(sketch, "E199.top", {"start": v(50.8, 576.56) * mm, "end": v(-50.8, 576.56) * mm});
            skLineSegment(sketch, "E199.left", {"start": v(50.8, 334.36) * mm, "end": v(50.8, 576.56) * mm});
            skLineSegment(sketch, "E199.right", {"start": v(-50.8, 334.36) * mm, "end": v(-50.8, 576.56) * mm});
            skPoint(sketch, "E199.middle", {"position": v(0, 430.51) * mm});
            skLineSegment(sketch, "E200.0", {"start": v(177.8, 576.56) * mm, "end": v(-177.8, 576.56) * mm, "construction": true});
            skArc(sketch, "E201", {"start": v(-50.8, 336.18) * mm, "mid": v(0, 284.46) * mm, "end": v(50.8, 336.18) * mm});
            skPoint(sketch, "E202.orphan", {"position": v(-50.8, 284.46) * mm});
            skPoint(sketch, "E203.orphan", {"position": v(50.8, 284.46) * mm});
            skSolve(sketch);
        }
        {
            var Q0;
            Q0=qSketchRegion(id+"F24",true);
            var Q1;
            Q1=makeQuery(id+"F8.opExtrude","CAP_FACE",FACE,{"disambiguationData":[OSD([sQuery(id+"F7.wireOp",EDGE,"E11.0"),sQuery(id+"F7.wireOp",EDGE,"E11.1"),sQuery(id+"F7.wireOp",EDGE,"E11.2"),sQuery(id+"F7.wireOp",EDGE,"E11.3")])],"isStart":false});
            extrude(context, id + "F25", {"entities" : qUnion([Q0]), "operationType" : NewBodyOperationType.REMOVE, "endBound" : BoundingType.THROUGH_ALL, "oppositeDirection" : true, "depth" : 25.4 * mm, "endBoundEntityFace" : qUnion([Q1]), "offsetDistance" : 25.4 * mm});
        }
        {
            var Q0;
            Q0=makeQuery(id+"F10.opExtrude","CAP_FACE",FACE,{"disambiguationData":[OSD([sQuery(id+"F7.wireOp",EDGE,"E11.0"),sQuery(id+"F7.wireOp",EDGE,"E11.3"),sQuery(id+"F9.wireOp",EDGE,"E12.0"),sQuery(id+"F9.wireOp",EDGE,"E13.0"),sQuery(id+"F9.wireOp",EDGE,"E14"),sQuery(id+"F9.wireOp",EDGE,"E15")])],"isStart":false});
            var sketch = newSketch(context, id + "F26", { "sketchPlane" : qUnion([Q0])});
            skLineSegment(sketch, "E204.0", {"start": v(0.18, 618.48) * mm, "end": v(138.18, 582.92) * mm});
            skLineSegment(sketch, "E204.1", {"start": v(0.18, 618.48) * mm, "end": v(0.18, 283.37) * mm});
            skLineSegment(sketch, "E204.2", {"start": v(138.18, 582.92) * mm, "end": v(55.54, 269.6) * mm});
            skLineSegment(sketch, "E204.3", {"start": v(54.84, 266.97) * mm, "end": v(-0.31, 281.51) * mm});
            skLineSegment(sketch, "E205", {"start": v(0.18, 283.37) * mm, "end": v(0.18, 281.38) * mm});
            skLineSegment(sketch, "E206", {"start": v(55.54, 269.6) * mm, "end": v(54.84, 266.97) * mm});
            skSolve(sketch);
        }
    });
